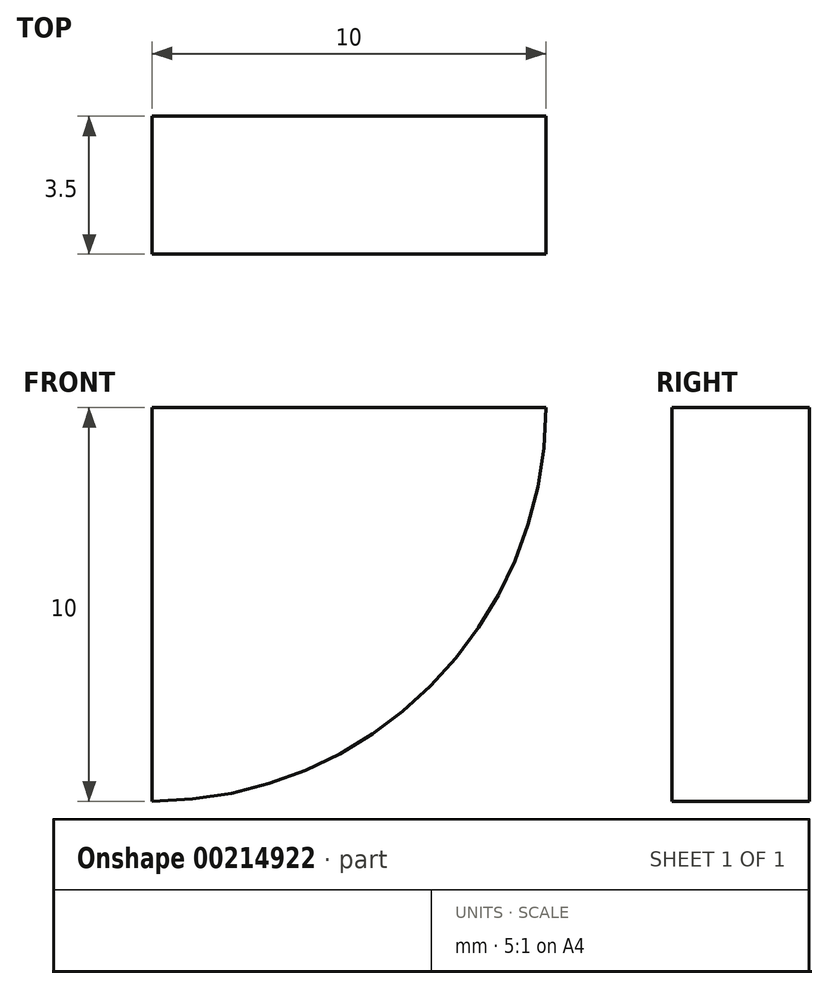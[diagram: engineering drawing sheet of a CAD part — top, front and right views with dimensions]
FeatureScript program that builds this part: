
annotation { "Feature Type Name" : "Feature", "Feature Type Description" : "" }
export const myFeature = defineFeature(function(context is Context, id is Id, definition is map)
    precondition{}
    {
        {
            var Q0;
            Q0=qCreatedBy(makeId("Front.planeOp"),FACE);
            var sketch = newSketch(context, id + "F0", { "sketchPlane" : qUnion([Q0])});
            skLineSegment(sketch, "E0.bottom", {"start": v(55, 30) * mm, "end": v(-55, 30) * mm});
            skLineSegment(sketch, "E0.top", {"start": v(55, -30) * mm, "end": v(-55, -30) * mm});
            skLineSegment(sketch, "E0.left", {"start": v(55, 30) * mm, "end": v(55, -30) * mm});
            skLineSegment(sketch, "E0.right", {"start": v(-55, 30) * mm, "end": v(-55, -30) * mm});
            skPoint(sketch, "E0.middle", {"position": v(0, 0) * mm});
            skArc(sketch, "E1", {"start": v(-45, 30) * mm, "mid": v(-47.93, 22.93) * mm, "end": v(-55, 20) * mm});
            skArc(sketch, "E2", {"start": v(-43, -30) * mm, "mid": v(-46.51, -21.51) * mm, "end": v(-55, -18) * mm});
            skArc(sketch, "E3", {"start": v(55, -20) * mm, "mid": v(47.93, -22.93) * mm, "end": v(45, -30) * mm});
            skArc(sketch, "E4", {"start": v(55, 20) * mm, "mid": v(47.93, 22.93) * mm, "end": v(45, 30) * mm});
            skLineSegment(sketch, "E5.bottom", {"start": v(50, 26) * mm, "end": v(-50, 26) * mm, "construction": true});
            skLineSegment(sketch, "E5.top", {"start": v(50, -26) * mm, "end": v(-50, -26) * mm, "construction": true});
            skLineSegment(sketch, "E5.left", {"start": v(50, 26) * mm, "end": v(50, -26) * mm, "construction": true});
            skLineSegment(sketch, "E5.right", {"start": v(-50, 26) * mm, "end": v(-50, -26) * mm, "construction": true});
            skSolve(sketch);
        }
        {
            var Q0;
            {var subQ0=sQuery(id+"F0.wireOp",EDGE,"E1");Q0=makeQuery(id+"F0.imprint","IMPRINT",FACE,{"disambiguationData":[TD([[makeQuery(id+"F0.imprint","IMPRINT",EDGE,{"derivedFrom":subQ0}),1.0]])]});}
            extrude(context, id + "F1", {"entities" : qUnion([Q0]), "depth" : 3.5 * mm, "offsetDistance" : 25 * mm});
        }
    });
